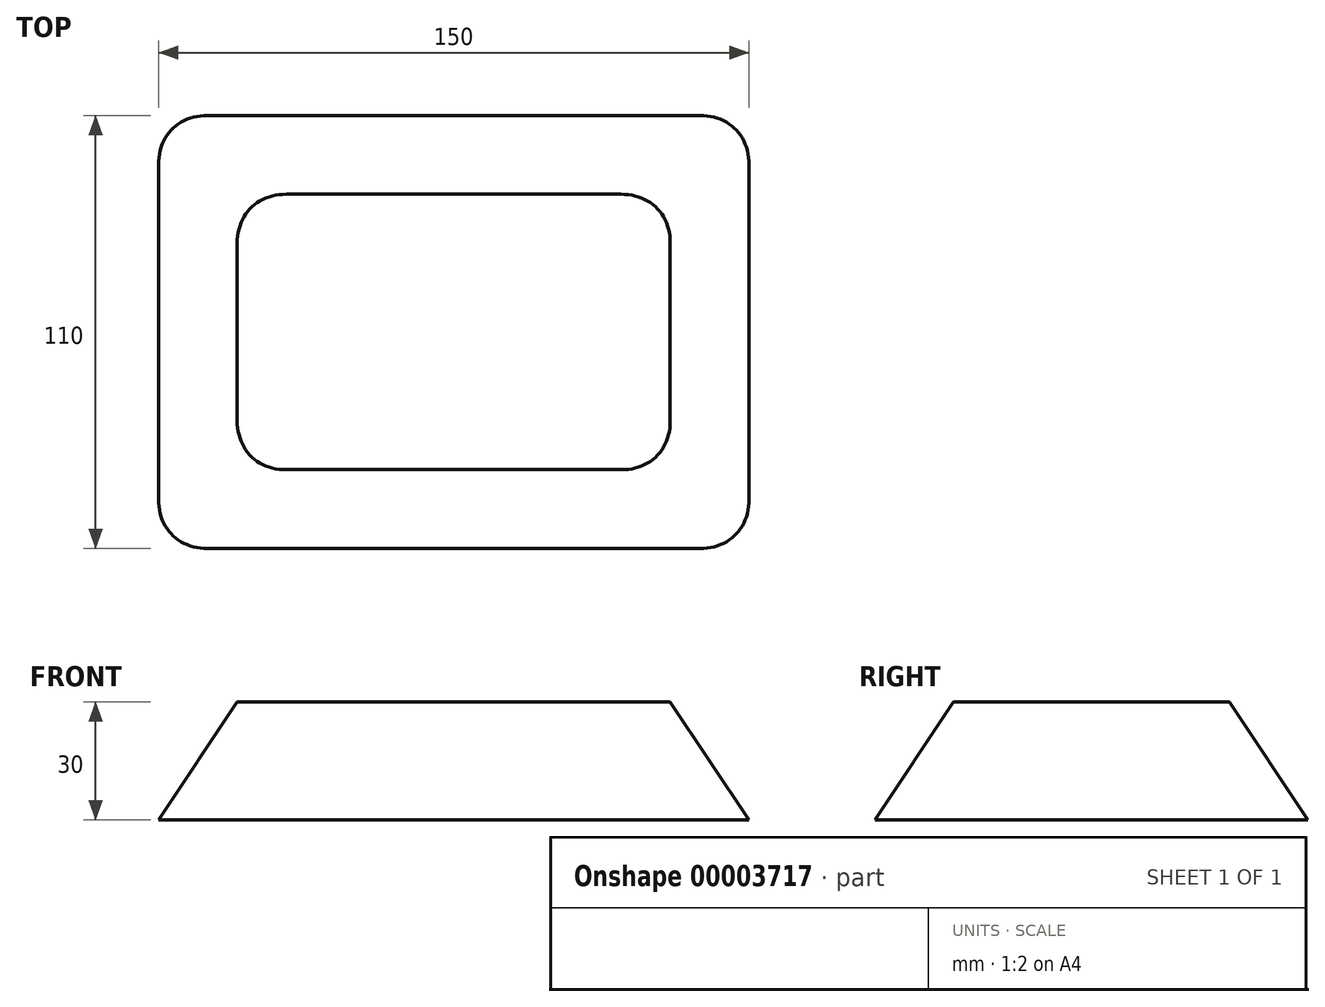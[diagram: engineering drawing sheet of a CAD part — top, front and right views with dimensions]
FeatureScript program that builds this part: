
annotation { "Feature Type Name" : "Feature", "Feature Type Description" : "" }
export const myFeature = defineFeature(function(context is Context, id is Id, definition is map)
    precondition{}
    {
        {
            var Q0;
            Q0=qCreatedBy(makeId("Top.planeOp"),FACE);
            var sketch = newSketch(context, id + "F0", { "sketchPlane" : qUnion([Q0])});
            skLineSegment(sketch, "E0.rect.bottom", {"start": v(75, 55) * mm, "end": v(-75, 55) * mm});
            skLineSegment(sketch, "E0.rect.top", {"start": v(75, -55) * mm, "end": v(-75, -55) * mm});
            skLineSegment(sketch, "E0.rect.left", {"start": v(75, 55) * mm, "end": v(75, -55) * mm});
            skLineSegment(sketch, "E0.rect.right", {"start": v(-75, 55) * mm, "end": v(-75, -55) * mm});
            skPoint(sketch, "E0.rect.middle", {"position": v(0, 0) * mm});
            skSolve(sketch);
        }
        {
            var Q0;
            Q0=qCreatedBy(makeId("Top.planeOp"),FACE);
            cPlane(context, id + "F1", {"entities" : qUnion([Q0]), "cplaneType" : CPlaneType.OFFSET, "offset" : 30 * mm, "width" : 150 * mm, "height" : 150 * mm});
        }
        {
            var Q0;
            Q0=qCreatedBy(id+"F1.planeOp",FACE);
            var sketch = newSketch(context, id + "F2", { "sketchPlane" : qUnion([Q0])});
            skLineSegment(sketch, "E1.rect.bottom", {"start": v(55, 35) * mm, "end": v(-55, 35) * mm});
            skLineSegment(sketch, "E1.rect.top", {"start": v(55, -35) * mm, "end": v(-55, -35) * mm});
            skLineSegment(sketch, "E1.rect.left", {"start": v(55, 35) * mm, "end": v(55, -35) * mm});
            skLineSegment(sketch, "E1.rect.right", {"start": v(-55, 35) * mm, "end": v(-55, -35) * mm});
            skPoint(sketch, "E1.rect.middle", {"position": v(0, 0) * mm});
            skSolve(sketch);
        }
        {
            var Q0;
            Q0=makeQuery(id+"F0.imprint","IMPRINT",FACE,{"disambiguationData":[TD([[makeQuery(id+"F0.imprint","IMPRINT",EDGE,{"derivedFrom":sQuery(id+"F0.wireOp",EDGE,"E0.rect.bottom")}),1.0]])]});
            var Q1;
            Q1=makeQuery(id+"F2.imprint","IMPRINT",FACE,{"disambiguationData":[TD([[makeQuery(id+"F2.imprint","IMPRINT",EDGE,{"derivedFrom":sQuery(id+"F2.wireOp",EDGE,"E1.rect.bottom")}),1.0]])]});
            loft(context, id + "F3", {"sheetProfilesArray" : [{ "sheetProfileEntities" : qUnion([Q0]) }, { "sheetProfileEntities" : qUnion([Q1]) }]});
        }
        {
            var Q0;
            Q0=makeQuery(id+"F3.opLoft","SWEPT_EDGE",EDGE,{"disambiguationData":[OSD([sQuery(id+"F0.wireOp",EDGE,"E0.rect.bottom"),sQuery(id+"F0.wireOp",EDGE,"E0.rect.left"),sQuery(id+"F2.wireOp",EDGE,"E1.rect.bottom"),sQuery(id+"F2.wireOp",EDGE,"E1.rect.left")])]});
            var Q1;
            Q1=makeQuery(id+"F3.opLoft","SWEPT_EDGE",EDGE,{"disambiguationData":[OSD([sQuery(id+"F0.wireOp",EDGE,"E0.rect.top"),sQuery(id+"F0.wireOp",EDGE,"E0.rect.left"),sQuery(id+"F2.wireOp",EDGE,"E1.rect.top"),sQuery(id+"F2.wireOp",EDGE,"E1.rect.left")])]});
            var Q2;
            Q2=makeQuery(id+"F3.opLoft","SWEPT_EDGE",EDGE,{"disambiguationData":[OSD([sQuery(id+"F0.wireOp",EDGE,"E0.rect.top"),sQuery(id+"F0.wireOp",EDGE,"E0.rect.right"),sQuery(id+"F2.wireOp",EDGE,"E1.rect.top"),sQuery(id+"F2.wireOp",EDGE,"E1.rect.right")])]});
            var Q3;
            Q3=makeQuery(id+"F3.opLoft","SWEPT_EDGE",EDGE,{"disambiguationData":[OSD([sQuery(id+"F0.wireOp",EDGE,"E0.rect.bottom"),sQuery(id+"F0.wireOp",EDGE,"E0.rect.right"),sQuery(id+"F2.wireOp",EDGE,"E1.rect.bottom"),sQuery(id+"F2.wireOp",EDGE,"E1.rect.right")])]});
            fillet(context, id + "F4", {"entities" : qUnion([Q0, Q1, Q2, Q3]), "radius" : 15 * mm, "tangentPropagation" : true, "allowEdgeOverflow" : false});
        }
    });
